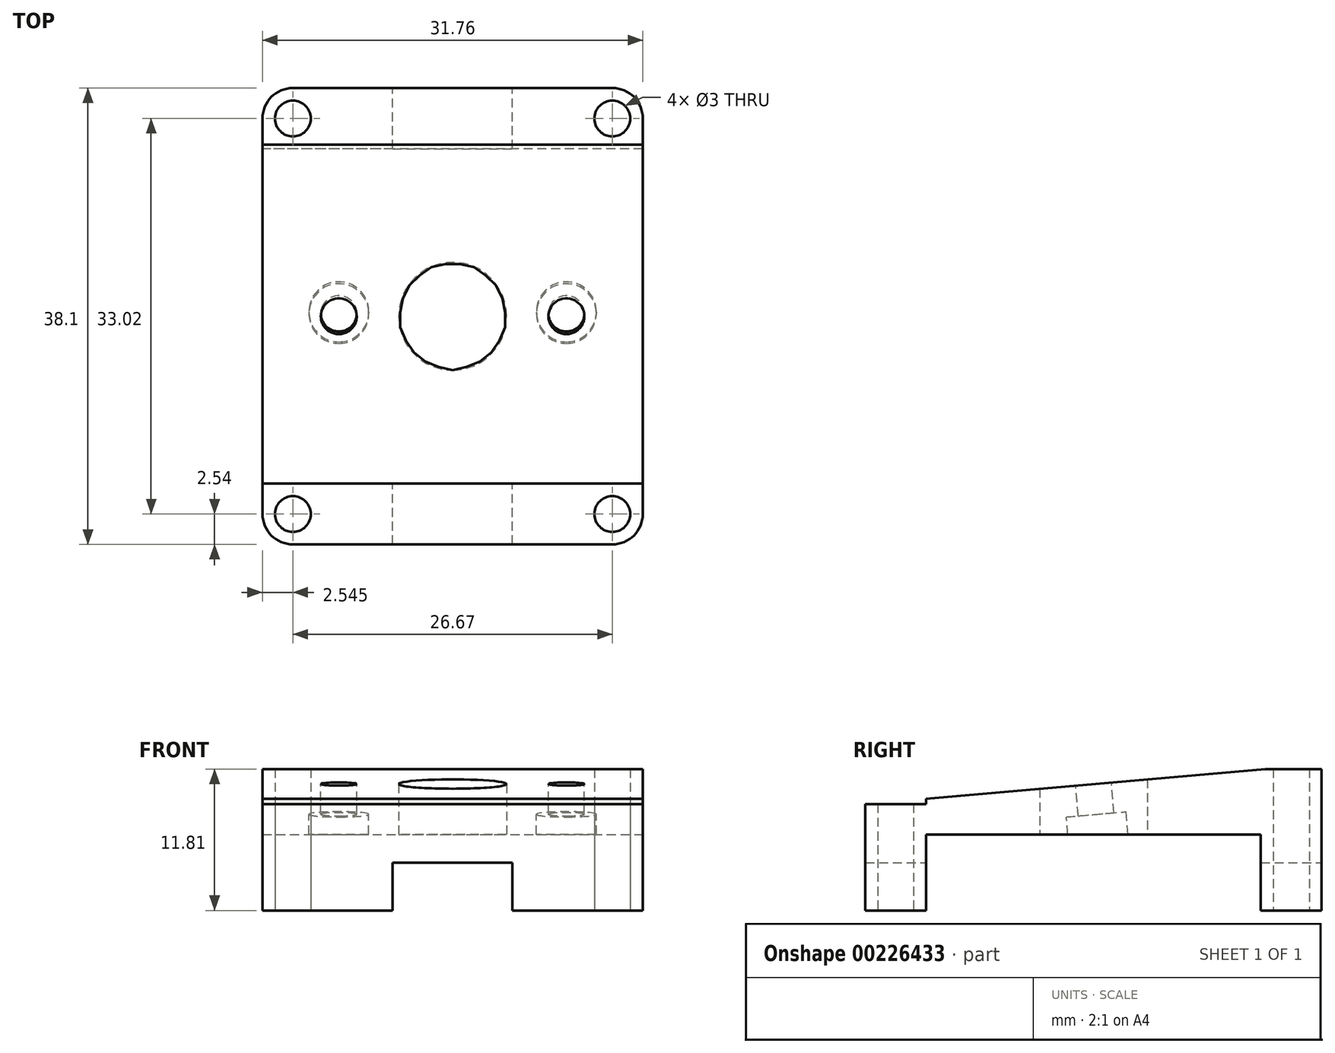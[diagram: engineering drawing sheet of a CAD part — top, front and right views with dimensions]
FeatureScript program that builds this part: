
annotation { "Feature Type Name" : "Feature", "Feature Type Description" : "" }
export const myFeature = defineFeature(function(context is Context, id is Id, definition is map)
    precondition{}
    {
        {
            var Q0;
            Q0=qCreatedBy(makeId("Top.planeOp"),FACE);
            var sketch = newSketch(context, id + "F0", { "sketchPlane" : qUnion([Q0])});
            skLineSegment(sketch, "E0.bottom", {"start": v(13.33, 19.05) * mm, "end": v(-13.34, 19.05) * mm});
            skLineSegment(sketch, "E0.top", {"start": v(13.34, -19.05) * mm, "end": v(-13.33, -19.05) * mm});
            skLineSegment(sketch, "E0.left", {"start": v(15.87, 16.51) * mm, "end": v(15.88, -16.51) * mm});
            skLineSegment(sketch, "E0.right", {"start": v(-15.88, 16.51) * mm, "end": v(-15.87, -16.51) * mm});
            skPoint(sketch, "E0.middle", {"position": v(0, 0) * mm});
            skCircle(sketch, "E1", {"center": v(0, 0) * mm, "radius": 9.5 * mm, "construction": true});
            skCircle(sketch, "E2", {"center": v(0, 0) * mm, "radius": 4.5 * mm});
            skPoint(sketch, "E3.visualSharp", {"position": v(-15.88, 19.05) * mm});
            skArc(sketch, "E3.filletArc", {"start": v(-13.34, 19.05) * mm, "mid": v(-15.13, 18.3) * mm, "end": v(-15.88, 16.51) * mm});
            skPoint(sketch, "E4.visualSharp", {"position": v(15.87, 19.05) * mm});
            skArc(sketch, "E4.filletArc", {"start": v(15.87, 16.51) * mm, "mid": v(15.13, 18.3) * mm, "end": v(13.33, 19.05) * mm});
            skPoint(sketch, "E5.visualSharp", {"position": v(15.88, -19.05) * mm});
            skArc(sketch, "E5.filletArc", {"start": v(13.34, -19.05) * mm, "mid": v(15.13, -18.3) * mm, "end": v(15.88, -16.51) * mm});
            skPoint(sketch, "E6.visualSharp", {"position": v(-15.87, -19.05) * mm});
            skArc(sketch, "E6.filletArc", {"start": v(-15.87, -16.51) * mm, "mid": v(-15.13, -18.3) * mm, "end": v(-13.33, -19.05) * mm});
            skCircle(sketch, "E7", {"center": v(-13.34, 16.51) * mm, "radius": 1.5 * mm});
            skCircle(sketch, "E8", {"center": v(13.33, 16.51) * mm, "radius": 1.5 * mm});
            skCircle(sketch, "E9", {"center": v(-13.33, -16.51) * mm, "radius": 1.5 * mm});
            skCircle(sketch, "E10", {"center": v(13.34, -16.51) * mm, "radius": 1.5 * mm});
            skCircle(sketch, "E11", {"center": v(0, 0) * mm, "radius": 13.5 * mm, "construction": true});
            skSolve(sketch);
        }
        {
            var Q0;
            Q0=makeQuery(id+"F0.imprint","IMPRINT",FACE,{"disambiguationData":[TD([[makeQuery(id+"F0.imprint","IMPRINT",EDGE,{"derivedFrom":sQuery(id+"F0.wireOp",EDGE,"E0.bottom")}),1.0]])]});
            extrude(context, id + "F1", {"entities" : qUnion([Q0]), "depth" : 2.54 * mm, "offsetDistance" : 25.4 * mm});
        }
        {
            var Q0;
            Q0=makeQuery(id+"F1.opExtrude","CAP_FACE",FACE,{"disambiguationData":[OSD([sQuery(id+"F0.wireOp",EDGE,"E0.bottom"),sQuery(id+"F0.wireOp",EDGE,"E0.top"),sQuery(id+"F0.wireOp",EDGE,"E0.left"),sQuery(id+"F0.wireOp",EDGE,"E0.right"),sQuery(id+"F0.wireOp",EDGE,"4kALpQac-FHhm-WEEX-tIft-xg5suqEFa5ex"),sQuery(id+"F0.wireOp",EDGE,"diZtlcp9-HFZ7-psaY-aWhu-X7GQ4Bjt7MnV"),sQuery(id+"F0.wireOp",EDGE,"E2"),sQuery(id+"F0.wireOp",EDGE,"E3.filletArc"),sQuery(id+"F0.wireOp",EDGE,"E4.filletArc"),sQuery(id+"F0.wireOp",EDGE,"E5.filletArc"),sQuery(id+"F0.wireOp",EDGE,"E6.filletArc"),sQuery(id+"F0.wireOp",EDGE,"E7"),sQuery(id+"F0.wireOp",EDGE,"E8"),sQuery(id+"F0.wireOp",EDGE,"E9"),sQuery(id+"F0.wireOp",EDGE,"E10")])],"isStart":true});
            var sketch = newSketch(context, id + "F2", { "sketchPlane" : qUnion([Q0])});
            skLineSegment(sketch, "E12", {"start": v(-15.87, 13.97) * mm, "end": v(15.88, 13.97) * mm});
            skLineSegment(sketch, "E13", {"start": v(15.87, -13.97) * mm, "end": v(-15.88, -13.97) * mm});
            skSolve(sketch);
        }
        {
            var Q0;
            {var subQ2=sQuery(id+"F2.wireOp",EDGE,"E12");Q0=makeQuery(id+"F2.imprint","IMPRINT",FACE,{"disambiguationData":[TD([[makeQuery(id+"F2.imprint","IMPRINT",EDGE,{"derivedFrom":subQ2}),1.0]])]});}
            var Q1;
            {var subQ3=sQuery(id+"F2.wireOp",EDGE,"E13");Q1=makeQuery(id+"F2.imprint","IMPRINT",FACE,{"disambiguationData":[TD([[makeQuery(id+"F2.imprint","IMPRINT",EDGE,{"derivedFrom":subQ3}),1.0]])]});}
            extrude(context, id + "F3", {"entities" : qUnion([Q0, Q1]), "operationType" : NewBodyOperationType.ADD, "depth" : 6.35 * mm, "offsetDistance" : 25.4 * mm});
        }
        {
            var Q0;
            {var subQ0=sQuery(id+"F0.wireOp",EDGE,"E0.bottom");Q0=makeQuery(id+"F3.boolean.opBoolean","MERGE",FACE,{"derivedFrom":[makeQuery(id+"F1.opExtrude","SWEPT_FACE",FACE,{"disambiguationData":[OSD([subQ0])]}),makeQuery(id+"F3.opExtrude","SWEPT_FACE",FACE,{"disambiguationData":[OSD([subQ0])]})]});}
            var sketch = newSketch(context, id + "F4", { "sketchPlane" : qUnion([Q0])});
            skLineSegment(sketch, "E14.bottom", {"start": v(5, -2.35) * mm, "end": v(-5, -2.35) * mm});
            skLineSegment(sketch, "E14.top", {"start": v(5, -10.35) * mm, "end": v(-5, -10.35) * mm});
            skLineSegment(sketch, "E14.left", {"start": v(5, -2.35) * mm, "end": v(5, -10.35) * mm});
            skLineSegment(sketch, "E14.right", {"start": v(-5, -2.35) * mm, "end": v(-5, -10.35) * mm});
            skPoint(sketch, "E14.middle", {"position": v(0, -6.35) * mm});
            skSolve(sketch);
        }
        {
            var Q0;
            {var subQ0=sQuery(id+"F4.wireOp",EDGE,"E14.bottom");Q0=makeQuery(id+"F4.imprint","IMPRINT",FACE,{"disambiguationData":[TD([[makeQuery(id+"F4.imprint","IMPRINT",EDGE,{"derivedFrom":subQ0}),1.0]])]});}
            extrude(context, id + "F5", {"entities" : qUnion([Q0]), "operationType" : NewBodyOperationType.REMOVE, "endBound" : BoundingType.THROUGH_ALL, "oppositeDirection" : true, "depth" : 25.4 * mm, "offsetDistance" : 25.4 * mm});
        }
        {
            var Q0;
            Q0=makeQuery(id+"F1.opExtrude","CAP_EDGE",EDGE,{"disambiguationData":[OSD([sQuery(id+"F0.wireOp",EDGE,"E0.top")])],"isStart":false});
            cPlane(context, id + "F6", {"entities" : qUnion([Q0]), "cplaneType" : CPlaneType.LINE_ANGLE, "offset" : 25.4 * mm, "angle" : 85 * degree, "width" : 152.4 * mm, "height" : 152.4 * mm});
        }
        {
            var Q0;
            Q0=makeQuery(id+"F1.opExtrude","CAP_FACE",FACE,{"disambiguationData":[OSD([sQuery(id+"F0.wireOp",EDGE,"E0.bottom"),sQuery(id+"F0.wireOp",EDGE,"E0.top"),sQuery(id+"F0.wireOp",EDGE,"E0.left"),sQuery(id+"F0.wireOp",EDGE,"E0.right"),sQuery(id+"F0.wireOp",EDGE,"4kALpQac-FHhm-WEEX-tIft-xg5suqEFa5ex"),sQuery(id+"F0.wireOp",EDGE,"diZtlcp9-HFZ7-psaY-aWhu-X7GQ4Bjt7MnV"),sQuery(id+"F0.wireOp",EDGE,"E2"),sQuery(id+"F0.wireOp",EDGE,"E3.filletArc"),sQuery(id+"F0.wireOp",EDGE,"E4.filletArc"),sQuery(id+"F0.wireOp",EDGE,"E5.filletArc"),sQuery(id+"F0.wireOp",EDGE,"E6.filletArc"),sQuery(id+"F0.wireOp",EDGE,"E7"),sQuery(id+"F0.wireOp",EDGE,"E8"),sQuery(id+"F0.wireOp",EDGE,"E9"),sQuery(id+"F0.wireOp",EDGE,"E10")])],"isStart":false});
            extrude(context, id + "F7", {"entities" : qUnion([Q0]), "operationType" : NewBodyOperationType.ADD, "depth" : 25.4 * mm, "offsetDistance" : 25.4 * mm});
        }
        {
            var Q0;
            Q0=qCreatedBy(id+"F6.planeOp",FACE);
            var sketch = newSketch(context, id + "F8", { "sketchPlane" : qUnion([Q0])});
            skLineSegment(sketch, "E15.bottom", {"start": v(-20.94, 22.51) * mm, "end": v(34.5, 22.51) * mm});
            skLineSegment(sketch, "E15.top", {"start": v(-20.94, -32.48) * mm, "end": v(34.5, -32.48) * mm});
            skLineSegment(sketch, "E15.left", {"start": v(-20.94, 22.51) * mm, "end": v(-20.94, -32.48) * mm});
            skLineSegment(sketch, "E15.right", {"start": v(34.5, 22.51) * mm, "end": v(34.5, -32.48) * mm});
            skSolve(sketch);
        }
        {
            var Q0;
            Q0=makeQuery(id+"F8.imprint","IMPRINT",FACE,{"disambiguationData":[TD([[makeQuery(id+"F8.imprint","IMPRINT",EDGE,{"derivedFrom":sQuery(id+"F8.wireOp",EDGE,"E15.bottom")}),-1.0]])]});
            extrude(context, id + "F9", {"entities" : qUnion([Q0]), "operationType" : NewBodyOperationType.REMOVE, "depth" : 25.4 * mm, "offsetDistance" : 25.4 * mm});
        }
        {
            var Q0;
            Q0=makeQuery(id+"F9.boolean.opBoolean","COPY",FACE,{"derivedFrom":makeQuery(id+"F9.opExtrude","CAP_FACE",FACE,{"disambiguationData":[OSD([sQuery(id+"F8.wireOp",EDGE,"E15.bottom"),sQuery(id+"F8.wireOp",EDGE,"E15.top"),sQuery(id+"F8.wireOp",EDGE,"E15.left"),sQuery(id+"F8.wireOp",EDGE,"E15.right")])],"isStart":true})});
            var sketch = newSketch(context, id + "F10", { "sketchPlane" : qUnion([Q0])});
            skLineSegment(sketch, "E16", {"start": v(9.5, 0.37) * mm, "end": v(-9.5, 0.37) * mm});
            skEllipse(sketch, "E17.0", {"center": v(0, 0.37) * mm, "majorRadius": 4.52 * mm, "minorRadius": 4.5 * mm, "majorAxis": v(0, -1)});
            skCircle(sketch, "E18", {"center": v(9.5, 0.37) * mm, "radius": 1.5 * mm});
            skCircle(sketch, "E19", {"center": v(-9.5, 0.37) * mm, "radius": 1.5 * mm});
            skSolve(sketch);
        }
        {
            var Q0;
            Q0=makeQuery(id+"F10.imprint","IMPRINT",FACE,{"disambiguationData":[TD([[makeQuery(id+"F10.imprint","IMPRINT",EDGE,{"derivedFrom":sQuery(id+"F10.wireOp",EDGE,"E19")}),1.0]])]});
            var Q1;
            Q1=makeQuery(id+"F10.imprint","IMPRINT",FACE,{"disambiguationData":[TD([[makeQuery(id+"F10.imprint","IMPRINT",EDGE,{"derivedFrom":sQuery(id+"F10.wireOp",EDGE,"E18")}),1.0]])]});
            extrude(context, id + "F11", {"entities" : qUnion([Q0, Q1]), "operationType" : NewBodyOperationType.REMOVE, "oppositeDirection" : true, "depth" : 25.4 * mm, "offsetDistance" : 25.4 * mm});
        }
        {
            var Q0;
            Q0=makeQuery(id+"F9.boolean.opBoolean","COPY",FACE,{"derivedFrom":makeQuery(id+"F9.opExtrude","CAP_FACE",FACE,{"disambiguationData":[OSD([sQuery(id+"F8.wireOp",EDGE,"E15.bottom"),sQuery(id+"F8.wireOp",EDGE,"E15.top"),sQuery(id+"F8.wireOp",EDGE,"E15.left"),sQuery(id+"F8.wireOp",EDGE,"E15.right")])],"isStart":true})});
            cPlane(context, id + "F12", {"entities" : qUnion([Q0]), "cplaneType" : CPlaneType.OFFSET, "offset" : 2.54 * mm, "oppositeDirection" : true, "width" : 152.4 * mm, "height" : 152.4 * mm});
        }
        {
            var Q0;
            Q0=qCreatedBy(id+"F12.planeOp",FACE);
            var sketch = newSketch(context, id + "F13", { "sketchPlane" : qUnion([Q0])});
            skCircle(sketch, "E20.0", {"center": v(-9.5, 0.37) * mm, "radius": 1.5 * mm});
            skCircle(sketch, "E21", {"center": v(-9.5, 0.37) * mm, "radius": 2.5 * mm});
            skCircle(sketch, "E22.0", {"center": v(9.5, 0.37) * mm, "radius": 1.5 * mm});
            skCircle(sketch, "E23", {"center": v(9.5, 0.37) * mm, "radius": 2.5 * mm});
            skSolve(sketch);
        }
        {
            var Q0;
            Q0 = qSketchRegion(id + "F13", true);
            extrude(context, id + "F14", {"entities" : qUnion([Q0]), "operationType" : NewBodyOperationType.REMOVE, "oppositeDirection" : true, "depth" : 25.4 * mm, "offsetDistance" : 25.4 * mm});
        }
        {
            var Q0;
            {var subQ0=sQuery(id+"F0.wireOp",EDGE,"E4.filletArc");var subQ1=sQuery(id+"F0.wireOp",EDGE,"E0.left");var subQ3=sQuery(id+"F2.wireOp",EDGE,"E13");var subQ4=sQuery(id+"F0.wireOp",EDGE,"E8");var subQ5=sQuery(id+"F0.wireOp",EDGE,"E0.bottom");Q0=makeQuery(id+"F5.boolean.opBoolean","SPLIT",FACE,{"disambiguationData":[TD([makeQuery(id+"F1.opExtrude","SWEPT_FACE",FACE,{"disambiguationData":[OSD([subQ1])]})])],"derivedFrom":makeQuery(id+"F3.opExtrude","CAP_FACE",FACE,{"disambiguationData":[OSD([subQ5,subQ1,sQuery(id+"F0.wireOp",EDGE,"E0.right"),sQuery(id+"F0.wireOp",EDGE,"E3.filletArc"),subQ0,sQuery(id+"F0.wireOp",EDGE,"E7"),subQ4,subQ3])],"isStart":false})});}
            cPlane(context, id + "F15", {"entities" : qUnion([Q0]), "cplaneType" : CPlaneType.OFFSET, "offset" : 11.8 * mm, "oppositeDirection" : true, "width" : 152.4 * mm, "height" : 152.4 * mm});
        }
        {
            var Q0;
            Q0=qCreatedBy(id+"F15.planeOp",FACE);
            var sketch = newSketch(context, id + "F16", { "sketchPlane" : qUnion([Q0])});
            skLineSegment(sketch, "E24.bottom", {"start": v(17.24, -12.78) * mm, "end": v(-29.03, -12.78) * mm});
            skLineSegment(sketch, "E24.top", {"start": v(17.24, -24.02) * mm, "end": v(-29.03, -24.02) * mm});
            skLineSegment(sketch, "E24.left", {"start": v(17.24, -12.78) * mm, "end": v(17.24, -24.02) * mm});
            skLineSegment(sketch, "E24.right", {"start": v(-29.03, -12.78) * mm, "end": v(-29.03, -24.02) * mm});
            skSolve(sketch);
        }
        {
            var Q0;
            Q0=makeQuery(id+"F16.imprint","IMPRINT",FACE,{"disambiguationData":[TD([[makeQuery(id+"F16.imprint","IMPRINT",EDGE,{"derivedFrom":sQuery(id+"F16.wireOp",EDGE,"E24.bottom")}),1.0]])]});
            extrude(context, id + "F17", {"entities" : qUnion([Q0]), "operationType" : NewBodyOperationType.REMOVE, "oppositeDirection" : true, "depth" : 25.4 * mm, "offsetDistance" : 25.4 * mm});
        }
        {
            var Q0;
            {var subQ0=sQuery(id+"F0.wireOp",EDGE,"E5.filletArc");var subQ1=sQuery(id+"F0.wireOp",EDGE,"E0.left");var subQ3=sQuery(id+"F2.wireOp",EDGE,"E12");var subQ4=sQuery(id+"F0.wireOp",EDGE,"E10");var subQ5=sQuery(id+"F0.wireOp",EDGE,"E0.top");Q0=makeQuery(id+"F5.boolean.opBoolean","SPLIT",FACE,{"disambiguationData":[TD([makeQuery(id+"F1.opExtrude","SWEPT_FACE",FACE,{"disambiguationData":[OSD([subQ1])]})])],"derivedFrom":makeQuery(id+"F3.opExtrude","CAP_FACE",FACE,{"disambiguationData":[OSD([subQ5,subQ1,sQuery(id+"F0.wireOp",EDGE,"E0.right"),subQ0,sQuery(id+"F0.wireOp",EDGE,"E6.filletArc"),sQuery(id+"F0.wireOp",EDGE,"E9"),subQ4,subQ3])],"isStart":false})});}
            cPlane(context, id + "F18", {"entities" : qUnion([Q0]), "cplaneType" : CPlaneType.OFFSET, "offset" : 8.9 * mm, "oppositeDirection" : true, "width" : 152.4 * mm, "height" : 152.4 * mm});
        }
        {
            var Q0;
            Q0=qCreatedBy(id+"F18.planeOp",FACE);
            var sketch = newSketch(context, id + "F19", { "sketchPlane" : qUnion([Q0])});
            skLineSegment(sketch, "E25.bottom", {"start": v(17.93, 19.05) * mm, "end": v(-15.87, 19.05) * mm});
            skLineSegment(sketch, "E25.top", {"start": v(17.93, 13.97) * mm, "end": v(-15.88, 13.97) * mm});
            skLineSegment(sketch, "E25.left", {"start": v(17.93, 19.05) * mm, "end": v(17.93, 13.97) * mm});
            skLineSegment(sketch, "E25.right", {"start": v(-15.87, 19.05) * mm, "end": v(-15.87, 13.97) * mm});
            skSolve(sketch);
        }
        {
            var Q0;
            Q0=makeQuery(id+"F19.imprint","IMPRINT",FACE,{"disambiguationData":[TD([[makeQuery(id+"F19.imprint","IMPRINT",EDGE,{"derivedFrom":sQuery(id+"F19.wireOp",EDGE,"E25.bottom")}),1.0]])]});
            extrude(context, id + "F20", {"entities" : qUnion([Q0]), "operationType" : NewBodyOperationType.REMOVE, "oppositeDirection" : true, "depth" : 25.4 * mm, "offsetDistance" : 25.4 * mm});
        }
    });
